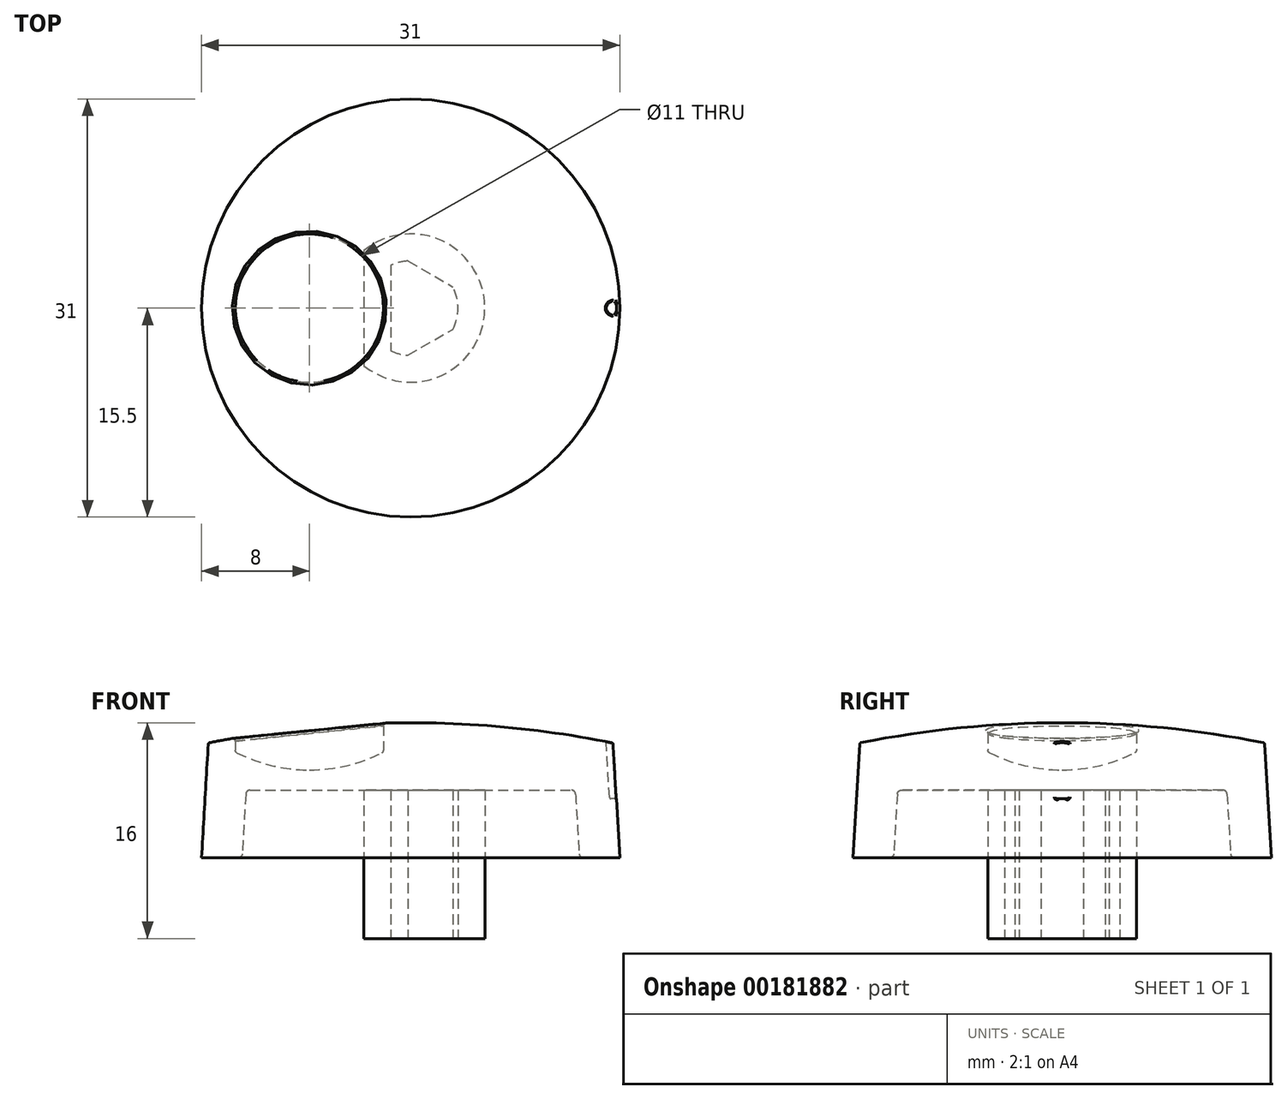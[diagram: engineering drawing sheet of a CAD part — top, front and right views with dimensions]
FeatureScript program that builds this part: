
annotation { "Feature Type Name" : "Feature", "Feature Type Description" : "" }
export const myFeature = defineFeature(function(context is Context, id is Id, definition is map)
    precondition{}
    {
        {
            assignVariable(context, id + "F0", {"name" : "height_above_panel", "anyValue" : 11});
        }
        {
            assignVariable(context, id + "F1", {"name" : "grip_depth_factor", "anyValue" : 0.75});
        }
        {
            var Q0;
            Q0=qCreatedBy(makeId("Top.planeOp"),FACE);
            var sketch = newSketch(context, id + "F2", { "sketchPlane" : qUnion([Q0])});
            skArc(sketch, "E0", {"start": v(-3.46, -4.27) * mm, "mid": v(5.5, 0) * mm, "end": v(-3.46, 4.27) * mm});
            skArc(sketch, "E1", {"start": v(-1.46, -2.62) * mm, "mid": v(3, 0.02) * mm, "end": v(-1.5, 2.6) * mm, "construction": true});
            skCircle(sketch, "E2", {"center": v(0, 0) * mm, "radius": 15.5 * mm, "construction": true});
            skLineSegment(sketch, "E3", {"start": v(-1.46, 3.18) * mm, "end": v(-1.46, -3.18) * mm});
            skLineSegment(sketch, "E4", {"start": v(-3.46, 4.27) * mm, "end": v(-3.46, -4.27) * mm});
            skArc(sketch, "E5", {"start": v(-1.46, -3.18) * mm, "mid": v(-0.85, -3.4) * mm, "end": v(-0.2, -3.5) * mm});
            skLineSegment(sketch, "E6", {"start": v(-0.2, -3.5) * mm, "end": v(3.13, -1.57) * mm});
            skArc(sketch, "E7.trimOffspring", {"start": v(3.13, -1.57) * mm, "mid": v(3.5, 0) * mm, "end": v(3.13, 1.57) * mm});
            skArc(sketch, "E8.trimOffspring", {"start": v(-0.2, 3.5) * mm, "mid": v(-0.85, 3.4) * mm, "end": v(-1.46, 3.18) * mm});
            skLineSegment(sketch, "E9.trimOffspring", {"start": v(-0.2, 3.5) * mm, "end": v(3.13, 1.57) * mm});
            skArc(sketch, "E10.0", {"start": v(-1.5, -2.51) * mm, "mid": v(2.92, -0.02) * mm, "end": v(-1.46, 2.53) * mm, "construction": true});
            skLineSegment(sketch, "E11", {"start": v(-1.5, 2.6) * mm, "end": v(-1.5, -2.51) * mm, "construction": true});
            skSolve(sketch);
        }
        {
            var Q0;
            Q0 = qSketchRegion(id + "F2", true);
            extrude(context, id + "F3", {"entities" : qUnion([Q0]), "depth" : 11 * mm});
        }
        {
            var Q0;
            Q0=qCreatedBy(makeId("Top.planeOp"),FACE);
            cPlane(context, id + "F4", {"entities" : qUnion([Q0]), "cplaneType" : CPlaneType.OFFSET, "offset" : 5 * mm, "width" : 150 * mm, "height" : 150 * mm});
        }
        {
            var Q0;
            Q0=qCreatedBy(makeId("Front.planeOp"),FACE);
            var sketch = newSketch(context, id + "F5", { "sketchPlane" : qUnion([Q0])});
            skLineSegment(sketch, "E12.0", {"start": v(-3.46, 11) * mm, "end": v(5.5, 11) * mm});
            skLineSegment(sketch, "E13", {"start": v(0, 11) * mm, "end": v(0, 16) * mm});
            skArc(sketch, "E14", {"start": v(15, 14.5) * mm, "mid": v(7.54, 15.62) * mm, "end": v(0, 16) * mm});
            skLineSegment(sketch, "E15", {"start": v(-10.14, 16) * mm, "end": v(12.68, 16) * mm, "construction": true});
            skLineSegment(sketch, "E16", {"start": v(15, 14.5) * mm, "end": v(15.5, 6) * mm});
            skLineSegment(sketch, "E17", {"start": v(15.5, 6) * mm, "end": v(12.5, 6) * mm});
            skLineSegment(sketch, "E18", {"start": v(12.5, 6) * mm, "end": v(12.2, 11) * mm});
            skLineSegment(sketch, "E19", {"start": v(5.5, 11) * mm, "end": v(12.2, 11) * mm});
            skSolve(sketch);
        }
        {
            var Q0;
            {var subQ0=sQuery(id+"F5.wireOp",EDGE,"E13");Q0=makeQuery(id+"F5.imprint","IMPRINT",FACE,{"disambiguationData":[TD([[makeQuery(id+"F5.imprint","IMPRINT",EDGE,{"derivedFrom":subQ0}),-1.0]])]});}
            var Q1;
            Q1=sQuery(id+"F5.wireOp",EDGE,"E13");
            revolve(context, id + "F6", {"operationType" : NewBodyOperationType.ADD, "entities" : qUnion([Q0]), "axis" : qUnion([Q1]), "revolveType" : RevolveType.FULL});
        }
        {
            var Q0;
            Q0=qCreatedBy(makeId("Front.planeOp"),FACE);
            var sketch = newSketch(context, id + "F7", { "sketchPlane" : qUnion([Q0])});
            skLineSegment(sketch, "E20.0", {"start": v(15, 14.5) * mm, "end": v(-15, 14.5) * mm});
            skLineSegment(sketch, "E21.bottom", {"start": v(-13, 24.51) * mm, "end": v(-7.5, 24.51) * mm});
            skLineSegment(sketch, "E21.top", {"start": v(-13, 13.83) * mm, "end": v(-7.5, 13.83) * mm});
            skLineSegment(sketch, "E21.left", {"start": v(-13, 24.51) * mm, "end": v(-13, 13.83) * mm});
            skLineSegment(sketch, "E21.right", {"start": v(-7.5, 24.51) * mm, "end": v(-7.5, 13.83) * mm});
            skLineSegment(sketch, "E22", {"start": v(-15.04, 12.5) * mm, "end": v(-4.86, 12.5) * mm, "construction": true});
            skArc(sketch, "E23", {"start": v(-13, 13.83) * mm, "mid": v(-10.33, 12.84) * mm, "end": v(-7.5, 12.5) * mm});
            skLineSegment(sketch, "E24", {"start": v(-7.5, 13.83) * mm, "end": v(-7.5, 12.5) * mm});
            skSolve(sketch);
        }
        {
            var Q0;
            Q0 = qSketchRegion(id + "F7", true);
            var Q1;
            Q1=sQuery(id+"F7.wireOp",EDGE,"E21.right");
            revolve(context, id + "F8", {"operationType" : NewBodyOperationType.REMOVE, "entities" : qUnion([Q0]), "axis" : qUnion([Q1]), "revolveType" : RevolveType.FULL, "oppositeDirection" : true});
        }
        {
            var Q0;
            Q0=sQuery(id+"F5.wireOp",EDGE,"E16");
            var Q1;
            Q1=sQuery(id+"F5.wireOp",VERTEX,"E16.start");
            cPlane(context, id + "F9", {"entities" : qUnion([Q0, Q1]), "cplaneType" : CPlaneType.LINE_POINT, "offset" : 25 * mm, "width" : 150 * mm, "height" : 150 * mm});
        }
        {
            var Q0;
            Q0=qCreatedBy(id+"F9.planeOp",FACE);
            var sketch = newSketch(context, id + "F10", { "sketchPlane" : qUnion([Q0])});
            skPoint(sketch, "E25.0", {"position": v(15.83, 0) * mm});
            skCircle(sketch, "E26", {"center": v(15.83, 0) * mm, "radius": 0.5 * mm});
            skSolve(sketch);
        }
        {
            var Q0;
            Q0=makeQuery(id+"F10.imprint","IMPRINT",FACE,{"disambiguationData":[TD([[makeQuery(id+"F10.imprint","IMPRINT",EDGE,{"derivedFrom":sQuery(id+"F10.wireOp",EDGE,"E26")}),1.0]])]});
            extrude(context, id + "F11", {"entities" : qUnion([Q0]), "operationType" : NewBodyOperationType.REMOVE, "endBound" : BoundingType.SYMMETRIC, "depth" : (getVariable(context, 'grip_depth_factor') * getVariable(context, 'height_above_panel')) * mm});
        }
        {
            var Q0;
            Q0=makeQuery(id+"F11.boolean.opBoolean","COPY",FACE,{"derivedFrom":makeQuery(id+"F11.opExtrude","SWEPT_FACE",FACE,{"disambiguationData":[OSD([sQuery(id+"F10.wireOp",EDGE,"E26")])]})});
            var Q1;
            Q1=makeQuery(id+"F6.opRevolve","SWEPT_EDGE",EDGE,{"disambiguationData":[OSD([sQuery(id+"F5.wireOp",EDGE,"E14"),sQuery(id+"F5.wireOp",EDGE,"E16")])]});
            fillet(context, id + "F12", {"entities" : qUnion([Q0, Q1]), "radius" : 0.1 * mm, "tangentPropagation" : true, "allowEdgeOverflow" : false});
        }
        {
            var Q0;
            Q0=makeQuery(id+"F8.boolean.opBoolean","INTERSECT",EDGE,{"derivedFrom":[makeQuery(id+"F6.opRevolve","SWEPT_FACE",FACE,{"disambiguationData":[OSD([sQuery(id+"F5.wireOp",EDGE,"E14")])]}),makeQuery(id+"F8.opRevolve","SWEPT_FACE",FACE,{"disambiguationData":[OSD([sQuery(id+"F7.wireOp",EDGE,"E21.left")])]})]});
            var Q1;
            Q1=makeQuery(id+"F8.boolean.opBoolean","COPY",EDGE,{"derivedFrom":makeQuery(id+"F8.opRevolve","SWEPT_EDGE",EDGE,{"disambiguationData":[OSD([sQuery(id+"F7.wireOp",EDGE,"E21.top"),sQuery(id+"F7.wireOp",EDGE,"E21.left"),sQuery(id+"F7.wireOp",EDGE,"E23")])]})});
            fillet(context, id + "F13", {"entities" : qUnion([Q0, Q1]), "radius" : 0.2 * mm, "tangentPropagation" : true, "allowEdgeOverflow" : false});
        }
        {
            var Q0;
            Q0=makeQuery(id+"F6.opRevolve","SWEPT_EDGE",EDGE,{"disambiguationData":[OSD([sQuery(id+"F5.wireOp",EDGE,"E18"),sQuery(id+"F5.wireOp",EDGE,"EPLxxkZY-Jm2v-z4IR-q4Ga-VjId1qaTgEh2")])]});
            var Q1;
            Q1=makeQuery(id+"F6.boolean.opBoolean","MERGE",EDGE,{"derivedFrom":[makeQuery(id+"F3.opExtrude","CAP_EDGE",EDGE,{"disambiguationData":[OSD([sQuery(id+"F2.wireOp",EDGE,"E0")])],"isStart":false}),makeQuery(id+"F6.opRevolve","SWEPT_EDGE",EDGE,{"disambiguationData":[OSD([sQuery(id+"F5.wireOp",EDGE,"E12.0"),sQuery(id+"F5.wireOp",EDGE,"EPLxxkZY-Jm2v-z4IR-q4Ga-VjId1qaTgEh2")])]})]});
            var Q2;
            Q2=makeQuery(id+"F3.opExtrude","CAP_EDGE",EDGE,{"disambiguationData":[OSD([sQuery(id+"F2.wireOp",EDGE,"E4")])],"isStart":false});
            fillet(context, id + "F14", {"entities" : qUnion([Q0, Q1, Q2]), "radius" : 0.3 * mm, "tangentPropagation" : true, "allowEdgeOverflow" : false});
        }
    });
